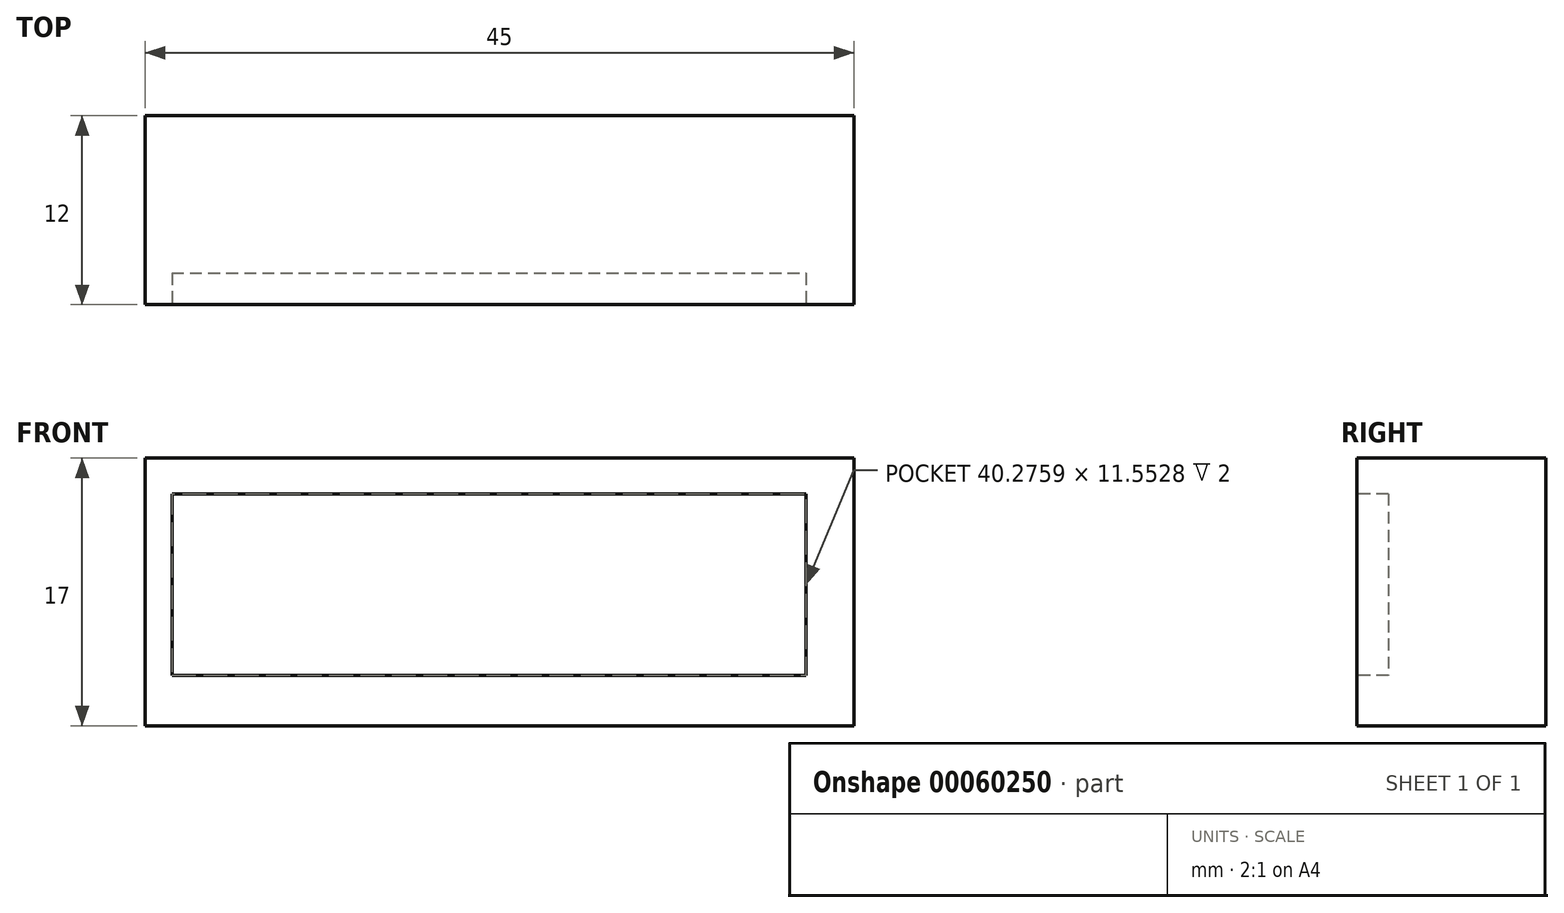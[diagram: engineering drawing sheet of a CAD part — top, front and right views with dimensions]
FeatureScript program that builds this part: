
annotation { "Feature Type Name" : "Feature", "Feature Type Description" : "" }
export const myFeature = defineFeature(function(context is Context, id is Id, definition is map)
    precondition{}
    {
        {
            var Q0;
            Q0=qCreatedBy(makeId("Front.planeOp"),FACE);
            var sketch = newSketch(context, id + "F0", { "sketchPlane" : qUnion([Q0])});
            skLineSegment(sketch, "E0.rect.bottom", {"start": v(22.5, 8.5) * mm, "end": v(-22.5, 8.5) * mm});
            skLineSegment(sketch, "E0.rect.top", {"start": v(22.5, -8.5) * mm, "end": v(-22.5, -8.5) * mm});
            skLineSegment(sketch, "E0.rect.left", {"start": v(22.5, 8.5) * mm, "end": v(22.5, -8.5) * mm});
            skLineSegment(sketch, "E0.rect.right", {"start": v(-22.5, 8.5) * mm, "end": v(-22.5, -8.5) * mm});
            skPoint(sketch, "E0.rect.middle", {"position": v(0, 0) * mm});
            skSolve(sketch);
        }
        {
            var Q0;
            Q0 = qSketchRegion(id + "F0", true);
            extrude(context, id + "F1", {"entities" : qUnion([Q0]), "depth" : 12 * mm});
        }
        {
            var Q0;
            Q0=makeQuery(id+"F1.opExtrude","CAP_FACE",FACE,{"disambiguationData":[OSD([sQuery(id+"F0.wireOp",EDGE,"E0.rect.bottom"),sQuery(id+"F0.wireOp",EDGE,"E0.rect.top"),sQuery(id+"F0.wireOp",EDGE,"E0.rect.left"),sQuery(id+"F0.wireOp",EDGE,"E0.rect.right")])],"isStart":false});
            var sketch = newSketch(context, id + "F2", { "sketchPlane" : qUnion([Q0])});
            skLineSegment(sketch, "E1.bottom", {"start": v(-20.8, 6.24) * mm, "end": v(19.47, 6.24) * mm});
            skLineSegment(sketch, "E1.top", {"start": v(-20.8, -5.32) * mm, "end": v(19.47, -5.32) * mm});
            skLineSegment(sketch, "E1.left", {"start": v(-20.8, 6.24) * mm, "end": v(-20.8, -5.32) * mm});
            skLineSegment(sketch, "E1.right", {"start": v(19.47, 6.24) * mm, "end": v(19.47, -5.32) * mm});
            skSolve(sketch);
        }
        {
            var Q0;
            Q0=makeQuery(id+"F2.imprint","IMPRINT",FACE,{"disambiguationData":[TD([[makeQuery(id+"F2.imprint","IMPRINT",EDGE,{"derivedFrom":sQuery(id+"F2.wireOp",EDGE,"E1.bottom")}),-1.0]])]});
            extrude(context, id + "F3", {"entities" : qUnion([Q0]), "operationType" : NewBodyOperationType.REMOVE, "oppositeDirection" : true, "depth" : 2 * mm});
        }
    });
